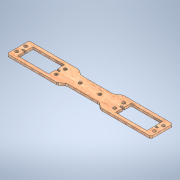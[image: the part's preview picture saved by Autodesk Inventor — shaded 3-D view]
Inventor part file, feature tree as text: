
AUTODESK INVENTOR PART (.ipt)
format: ipt  version: 2022 (Build 260153000, 153)  size: 232,960 bytes
history: native  units: mm
features: reference x11, other x5, extrude x1, sketch x1
ambient origin geometry x8: Origin, YZ Plane, XZ Plane, XY Plane, X Axis, Y Axis, Z Axis, Center Point
bodies: Solid1 (feature_tree)
feature tree (18):
  extrude  "Extrusion1"  Depth=9.0mm
  sketch  "Sketch1"  dims[d19=12.5mm d20=9.0mm d21=9.0mm d22=14.0mm d23=14.0mm d25=5.0mm d26=91.5mm d29=40.0mm d30=20.0mm d31=4.0mm d33=3.0mm d34=0.0mm d35=2.0mm d36=5.0mm d37=5.0mm d38=5.0mm d39=5.0mm d40=5.0mm d41=5.0mm d42=5.0mm d43=5.0mm d44=3.9mm d45=3.9mm d46=3.9mm d47=3.9mm d48=3.9mm d49=3.9mm d50=3.9mm d51=3.9mm d52=125.0mm d53=40.0mm d54=9.0mm d55=4.0mm d56=2.0mm d57=4.0mm d58=9.0mm d59=4.0mm d60=2.0mm d61=4.0mm d62=9.0mm d63=9.0mm d64=4.0mm d65=2.0mm d66=4.0mm d67=9.0mm d68=9.0mm d69=4.0mm d70=2.0mm d71=4.0mm d72=9.0mm d73=25.0mm d74=0.5mm d75=0.872665mm d76=0.5mm d77=0.872665mm]
  reference  "Reference1"
  reference  "Reference2"
  reference  "Reference3"
  reference  "Reference4"
  reference  "Reference5"
  reference  "Reference6"
  reference  "Reference7"
  reference  "Reference8"
  reference  "Reference9"
  reference  "Reference10"
  reference  "Reference11"
  other  "<userpath>\rob.iam"
  other  "rob.iam"
  other  "Motor Mg995:3"
  other  "Motor Mg995:4"
  other  "Estella Servo1:1"
